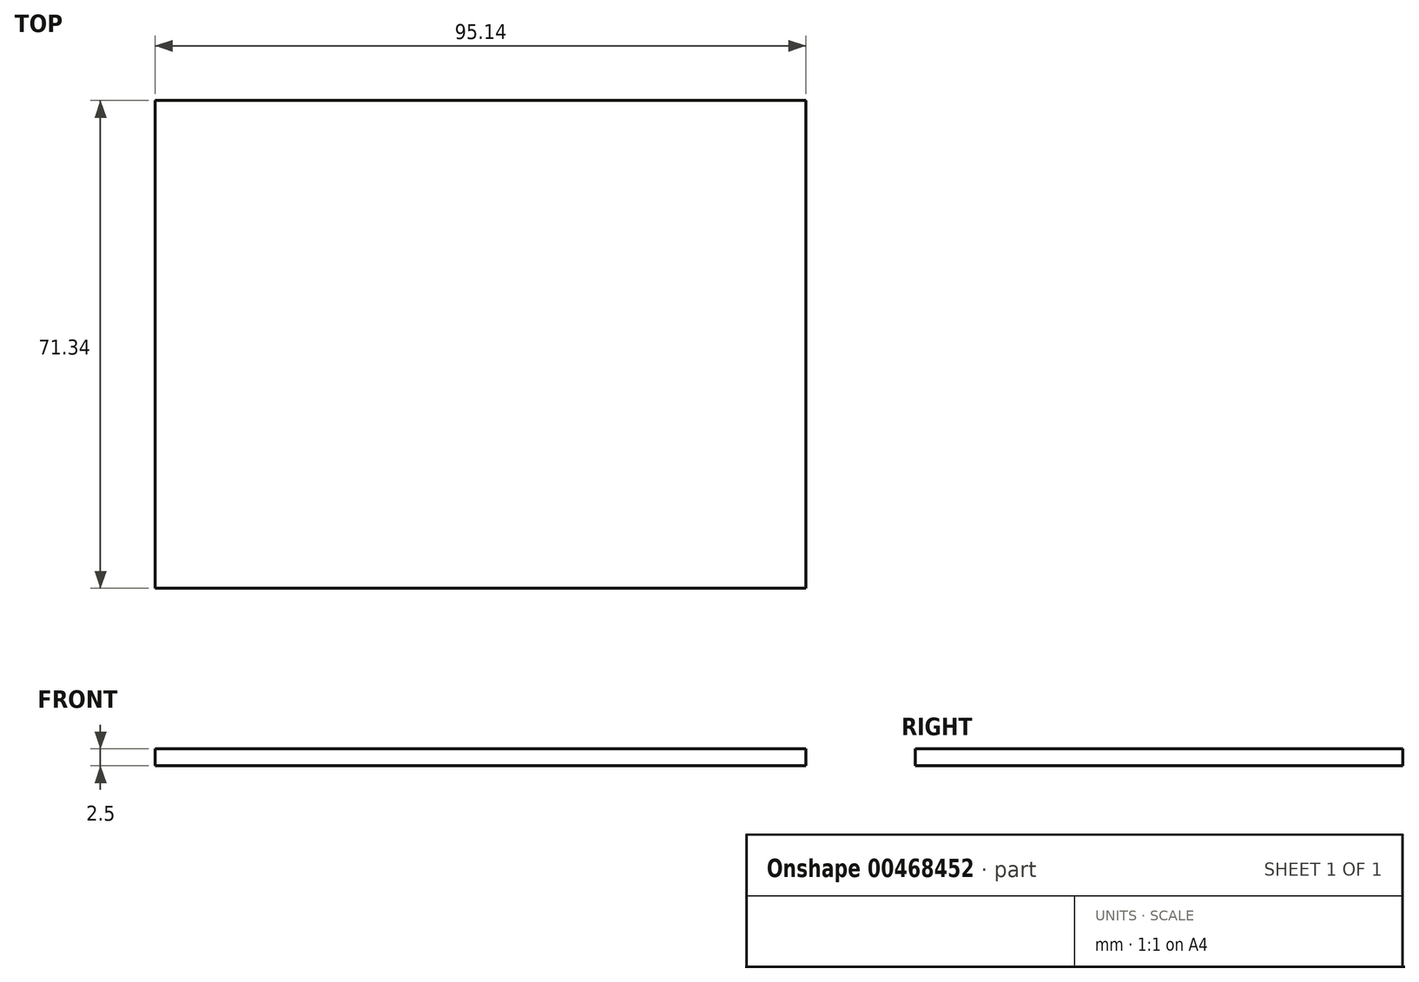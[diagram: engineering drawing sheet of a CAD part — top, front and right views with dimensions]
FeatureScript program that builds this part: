
annotation { "Feature Type Name" : "Feature", "Feature Type Description" : "" }
export const myFeature = defineFeature(function(context is Context, id is Id, definition is map)
    precondition{}
    {
        {
            var Q0;
            Q0=qCreatedBy(makeId("Top.planeOp"),FACE);
            var sketch = newSketch(context, id + "F0", { "sketchPlane" : qUnion([Q0])});
            skLineSegment(sketch, "E0.bottom", {"start": v(42.18, -30.27) * mm, "end": v(-42.17, -30.28) * mm});
            skLineSegment(sketch, "E0.top", {"start": v(42.17, 30.27) * mm, "end": v(-42.18, 30.27) * mm});
            skLineSegment(sketch, "E0.left", {"start": v(42.18, -30.27) * mm, "end": v(42.17, 30.28) * mm});
            skLineSegment(sketch, "E0.right", {"start": v(-42.17, -30.28) * mm, "end": v(-42.18, 30.27) * mm});
            skPoint(sketch, "E0.middle", {"position": v(0, 0) * mm});
            skLineSegment(sketch, "E1.bottom", {"start": v(-47.57, 35.67) * mm, "end": v(47.57, 35.67) * mm});
            skLineSegment(sketch, "E1.top", {"start": v(-47.57, -35.67) * mm, "end": v(47.57, -35.67) * mm});
            skLineSegment(sketch, "E1.left", {"start": v(-47.57, 35.67) * mm, "end": v(-47.57, -35.67) * mm});
            skLineSegment(sketch, "E1.right", {"start": v(47.57, 35.67) * mm, "end": v(47.57, -35.67) * mm});
            skLineSegment(sketch, "E2.bottom", {"start": v(50.07, 38.17) * mm, "end": v(-50.07, 38.17) * mm});
            skLineSegment(sketch, "E2.top", {"start": v(50.07, -38.17) * mm, "end": v(-50.07, -38.17) * mm});
            skLineSegment(sketch, "E2.left", {"start": v(50.07, 38.17) * mm, "end": v(50.07, -38.17) * mm});
            skLineSegment(sketch, "E2.right", {"start": v(-50.07, 38.17) * mm, "end": v(-50.07, -38.17) * mm});
            skSolve(sketch);
        }
        {
            var Q0;
            Q0=makeQuery(id+"F0.imprint","IMPRINT",FACE,{"disambiguationData":[TD([[makeQuery(id+"F0.imprint","IMPRINT",EDGE,{"derivedFrom":sQuery(id+"F0.wireOp",EDGE,"E0.bottom")}),1.0]])]});
            var Q1;
            Q1=makeQuery(id+"F0.imprint","IMPRINT",FACE,{"disambiguationData":[TD([[makeQuery(id+"F0.imprint","IMPRINT",EDGE,{"derivedFrom":sQuery(id+"F0.wireOp",EDGE,"E0.bottom")}),-1.0]])]});
            extrude(context, id + "F1", {"entities" : qUnion([Q0, Q1]), "depth" : 2.5 * mm});
        }
    });
